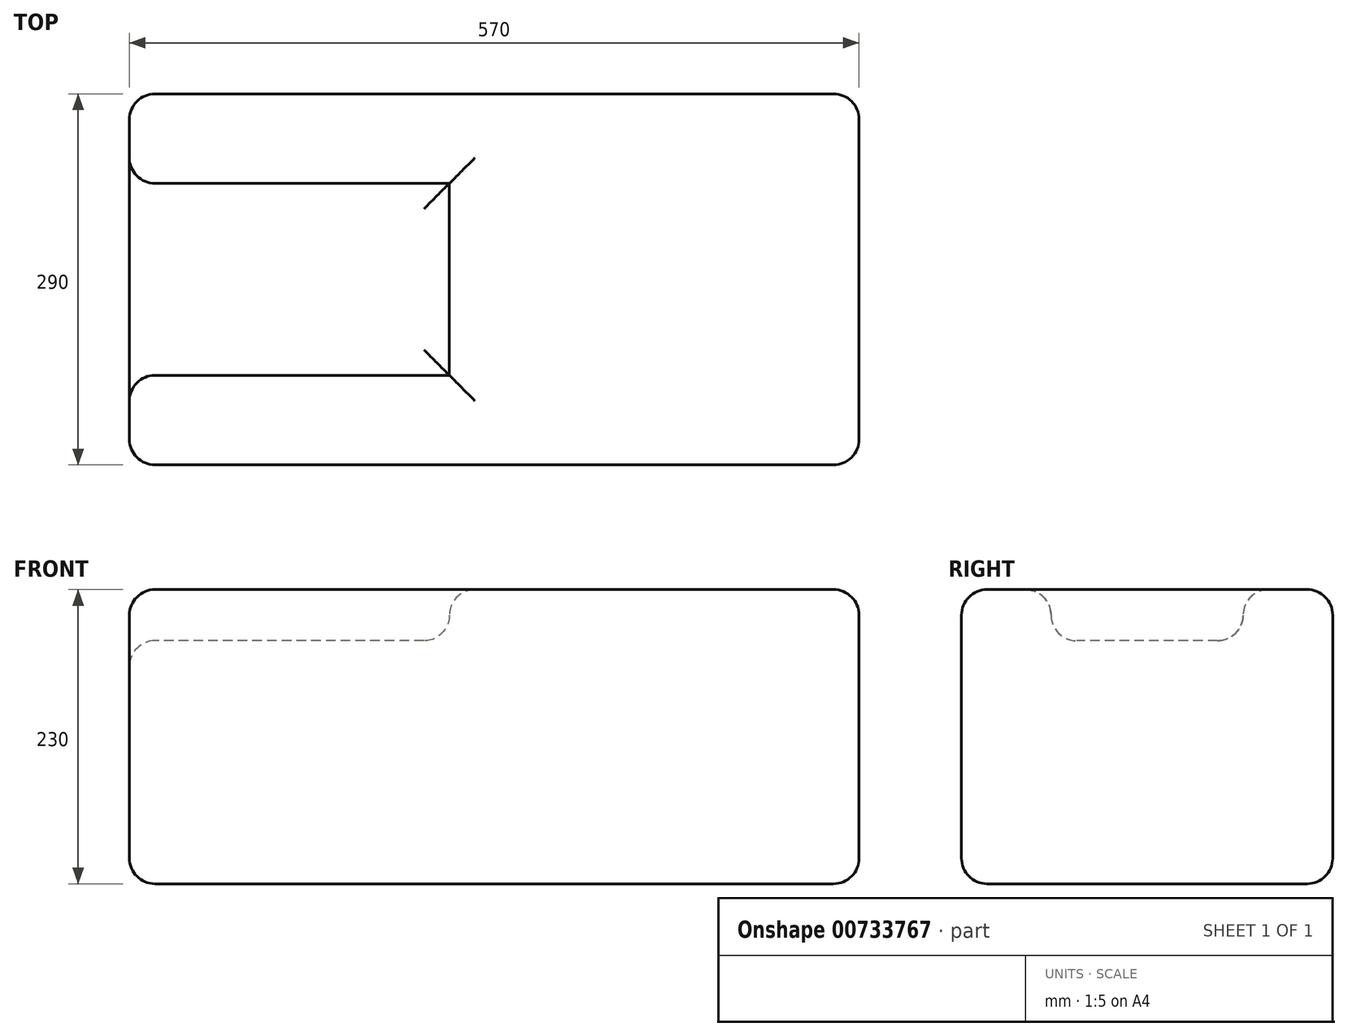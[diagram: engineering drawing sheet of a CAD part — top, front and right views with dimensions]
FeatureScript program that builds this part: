
annotation { "Feature Type Name" : "Feature", "Feature Type Description" : "" }
export const myFeature = defineFeature(function(context is Context, id is Id, definition is map)
    precondition{}
    {
        {
            var Q0;
            Q0=qCreatedBy(makeId("Top.planeOp"),FACE);
            var sketch = newSketch(context, id + "F0", { "sketchPlane" : qUnion([Q0])});
            skLineSegment(sketch, "E0.bottom", {"start": v(0, 0) * mm, "end": v(570, 0) * mm});
            skLineSegment(sketch, "E0.top", {"start": v(0, -290) * mm, "end": v(570, -290) * mm});
            skLineSegment(sketch, "E0.left", {"start": v(0, 0) * mm, "end": v(0, -290) * mm});
            skLineSegment(sketch, "E0.right", {"start": v(570, 0) * mm, "end": v(570, -290) * mm});
            skSolve(sketch);
        }
        {
            var Q0;
            Q0=makeQuery(id+"F0.imprint","IMPRINT",FACE,{"disambiguationData":[TD([[makeQuery(id+"F0.imprint","IMPRINT",EDGE,{"derivedFrom":sQuery(id+"F0.wireOp",EDGE,"E0.bottom")}),-1.0]])]});
            extrude(context, id + "F1", {"entities" : qUnion([Q0]), "depth" : 230 * mm, "offsetDistance" : 25 * mm});
        }
        {
            var Q0;
            Q0=makeQuery(id+"F1.opExtrude","CAP_FACE",FACE,{"disambiguationData":[OSD([sQuery(id+"F0.wireOp",EDGE,"E0.bottom"),sQuery(id+"F0.wireOp",EDGE,"E0.top"),sQuery(id+"F0.wireOp",EDGE,"E0.left"),sQuery(id+"F0.wireOp",EDGE,"E0.right")])],"isStart":false});
            var sketch = newSketch(context, id + "F2", { "sketchPlane" : qUnion([Q0])});
            skLineSegment(sketch, "E1.top", {"start": v(250, -220) * mm, "end": v(0, -220) * mm});
            skLineSegment(sketch, "E1.left", {"start": v(250, -145) * mm, "end": v(250, -220) * mm});
            skLineSegment(sketch, "E1.right", {"start": v(0, -145) * mm, "end": v(0, -220) * mm});
            skLineSegment(sketch, "E2.MirrorCS", {"start": v(250, -70) * mm, "end": v(0, -70) * mm});
            skLineSegment(sketch, "E3", {"start": v(250, -145) * mm, "end": v(250, -70) * mm});
            skSolve(sketch);
        }
        {
            var Q0;
            Q0=makeQuery(id+"F2.imprint","IMPRINT",FACE,{"disambiguationData":[TD([[makeQuery(id+"F2.imprint","IMPRINT",EDGE,{"derivedFrom":sQuery(id+"F2.wireOp",EDGE,"E1.top")}),-1.0]])]});
            extrude(context, id + "F3", {"entities" : qUnion([Q0]), "operationType" : NewBodyOperationType.REMOVE, "oppositeDirection" : true, "depth" : 40 * mm, "offsetDistance" : 25 * mm});
        }
        {
            var Q0;
            Q0=makeQuery(id+"F1.opExtrude","SWEPT_FACE",FACE,{"disambiguationData":[OSD([sQuery(id+"F0.wireOp",EDGE,"E0.left")])]});
            var Q1;
            Q1=makeQuery(id+"F1.opExtrude","SWEPT_FACE",FACE,{"disambiguationData":[OSD([sQuery(id+"F0.wireOp",EDGE,"E0.right")])]});
            var Q2;
            Q2=makeQuery(id+"F1.opExtrude","SWEPT_FACE",FACE,{"disambiguationData":[OSD([sQuery(id+"F0.wireOp",EDGE,"E0.top")])]});
            var Q3;
            Q3=makeQuery(id+"F1.opExtrude","SWEPT_FACE",FACE,{"disambiguationData":[OSD([sQuery(id+"F0.wireOp",EDGE,"E0.bottom")])]});
            var Q4;
            Q4=makeQuery(id+"F3.boolean.opBoolean","COPY",FACE,{"derivedFrom":makeQuery(id+"F3.opExtrude","CAP_FACE",FACE,{"disambiguationData":[OSD([sQuery(id+"F0.wireOp",EDGE,"E0.left"),sQuery(id+"F2.wireOp",EDGE,"E1.top"),sQuery(id+"F2.wireOp",EDGE,"E1.left"),sQuery(id+"F2.wireOp",EDGE,"E1.right"),sQuery(id+"F2.wireOp",EDGE,"E2.MirrorCS"),sQuery(id+"F2.wireOp",EDGE,"E3")])],"isStart":false})});
            var Q5;
            Q5=makeQuery(id+"F3.boolean.opBoolean","COPY",EDGE,{"derivedFrom":makeQuery(id+"F3.opExtrude","CAP_EDGE",EDGE,{"disambiguationData":[OSD([sQuery(id+"F2.wireOp",EDGE,"E1.top")])],"isStart":true})});
            var Q6;
            Q6=makeQuery(id+"F3.boolean.opBoolean","COPY",EDGE,{"derivedFrom":makeQuery(id+"F3.opExtrude","CAP_EDGE",EDGE,{"disambiguationData":[OSD([sQuery(id+"F2.wireOp",EDGE,"E1.left"),sQuery(id+"F2.wireOp",EDGE,"E3")])],"isStart":true})});
            var Q7;
            Q7=makeQuery(id+"F3.boolean.opBoolean","COPY",EDGE,{"derivedFrom":makeQuery(id+"F3.opExtrude","CAP_EDGE",EDGE,{"disambiguationData":[OSD([sQuery(id+"F2.wireOp",EDGE,"E2.MirrorCS")])],"isStart":true})});
            fillet(context, id + "F4", {"entities" : qUnion([Q0, Q1, Q2, Q3, Q4, Q5, Q6, Q7]), "radius" : 20 * mm, "allowEdgeOverflow" : false});
        }
        {
            var Q0;
            Q0=makeQuery(id+"F3.boolean.opBoolean","COPY",EDGE,{"derivedFrom":makeQuery(id+"F3.opExtrude","CAP_EDGE",EDGE,{"disambiguationData":[OSD([sQuery(id+"F2.wireOp",EDGE,"E2.MirrorCS")])],"isStart":true})});
            var Q1;
            Q1=makeQuery(id+"F3.boolean.opBoolean","COPY",EDGE,{"derivedFrom":makeQuery(id+"F3.opExtrude","CAP_EDGE",EDGE,{"disambiguationData":[OSD([sQuery(id+"F2.wireOp",EDGE,"E1.left"),sQuery(id+"F2.wireOp",EDGE,"E3")])],"isStart":true})});
            var Q2;
            Q2=makeQuery(id+"F3.boolean.opBoolean","COPY",EDGE,{"derivedFrom":makeQuery(id+"F3.opExtrude","CAP_EDGE",EDGE,{"disambiguationData":[OSD([sQuery(id+"F2.wireOp",EDGE,"E1.top")])],"isStart":true})});
            var Q3;
            Q3=makeQuery(id+"F3.boolean.opBoolean","COPY",EDGE,{"derivedFrom":makeQuery(id+"F3.opExtrude","CAP_EDGE",EDGE,{"disambiguationData":[OSD([sQuery(id+"F2.wireOp",EDGE,"E1.left"),sQuery(id+"F2.wireOp",EDGE,"E3")])],"isStart":false})});
            var Q4;
            Q4=makeQuery(id+"F3.boolean.opBoolean","COPY",EDGE,{"derivedFrom":makeQuery(id+"F3.opExtrude","CAP_EDGE",EDGE,{"disambiguationData":[OSD([sQuery(id+"F2.wireOp",EDGE,"E1.top")])],"isStart":false})});
            var Q5;
            Q5=makeQuery(id+"F3.boolean.opBoolean","COPY",EDGE,{"derivedFrom":makeQuery(id+"F3.opExtrude","CAP_EDGE",EDGE,{"disambiguationData":[OSD([sQuery(id+"F2.wireOp",EDGE,"E2.MirrorCS")])],"isStart":false})});
            var Q6;
            {var subQ0=sQuery(id+"F0.wireOp",EDGE,"E0.left");var subQ1=sQuery(id+"F0.wireOp",EDGE,"E0.top");Q6=makeQuery(id+"F3.boolean.opBoolean","SPLIT",EDGE,{"disambiguationData":[TD([makeQuery(id+"F1.opExtrude","SWEPT_FACE",FACE,{"disambiguationData":[OSD([subQ1])]})])],"derivedFrom":makeQuery(id+"F1.opExtrude","CAP_EDGE",EDGE,{"disambiguationData":[OSD([subQ0])],"isStart":false})});}
            var Q7;
            {var subQ0=sQuery(id+"F0.wireOp",EDGE,"E0.bottom");var subQ1=sQuery(id+"F0.wireOp",EDGE,"E0.left");Q7=makeQuery(id+"F3.boolean.opBoolean","SPLIT",EDGE,{"disambiguationData":[TD([makeQuery(id+"F1.opExtrude","SWEPT_FACE",FACE,{"disambiguationData":[OSD([subQ0])]})])],"derivedFrom":makeQuery(id+"F1.opExtrude","CAP_EDGE",EDGE,{"disambiguationData":[OSD([subQ1])],"isStart":false})});}
            var Q8;
            Q8=makeQuery(id+"F1.opExtrude","CAP_EDGE",EDGE,{"disambiguationData":[OSD([sQuery(id+"F0.wireOp",EDGE,"E0.top")])],"isStart":false});
            var Q9;
            Q9=makeQuery(id+"F1.opExtrude","CAP_FACE",FACE,{"disambiguationData":[OSD([sQuery(id+"F0.wireOp",EDGE,"E0.bottom"),sQuery(id+"F0.wireOp",EDGE,"E0.top"),sQuery(id+"F0.wireOp",EDGE,"E0.left"),sQuery(id+"F0.wireOp",EDGE,"E0.right")])],"isStart":false});
            var Q10;
            Q10=makeQuery(id+"F1.opExtrude","SWEPT_EDGE",EDGE,{"disambiguationData":[OSD([sQuery(id+"F0.wireOp",EDGE,"E0.top"),sQuery(id+"F0.wireOp",EDGE,"E0.right")])]});
            var Q11;
            Q11=makeQuery(id+"F1.opExtrude","SWEPT_EDGE",EDGE,{"disambiguationData":[OSD([sQuery(id+"F0.wireOp",EDGE,"E0.bottom"),sQuery(id+"F0.wireOp",EDGE,"E0.right")])]});
            var Q12;
            Q12=makeQuery(id+"F1.opExtrude","CAP_EDGE",EDGE,{"disambiguationData":[OSD([sQuery(id+"F0.wireOp",EDGE,"E0.right")])],"isStart":true});
            var Q13;
            Q13=makeQuery(id+"F1.opExtrude","CAP_EDGE",EDGE,{"disambiguationData":[OSD([sQuery(id+"F0.wireOp",EDGE,"E0.bottom")])],"isStart":true});
            var Q14;
            Q14=makeQuery(id+"F1.opExtrude","SWEPT_EDGE",EDGE,{"disambiguationData":[OSD([sQuery(id+"F0.wireOp",EDGE,"E0.bottom"),sQuery(id+"F0.wireOp",EDGE,"E0.left")])]});
            var Q15;
            Q15=makeQuery(id+"F1.opExtrude","CAP_EDGE",EDGE,{"disambiguationData":[OSD([sQuery(id+"F0.wireOp",EDGE,"E0.left")])],"isStart":true});
            var Q16;
            Q16=makeQuery(id+"F1.opExtrude","CAP_EDGE",EDGE,{"disambiguationData":[OSD([sQuery(id+"F0.wireOp",EDGE,"E0.top")])],"isStart":true});
            var Q17;
            Q17=makeQuery(id+"F1.opExtrude","SWEPT_EDGE",EDGE,{"disambiguationData":[OSD([sQuery(id+"F0.wireOp",EDGE,"E0.top"),sQuery(id+"F0.wireOp",EDGE,"E0.left")])]});
            var Q18;
            Q18=makeQuery(id+"F3.boolean.opBoolean","COPY",EDGE,{"derivedFrom":makeQuery(id+"F3.opExtrude","CAP_EDGE",EDGE,{"disambiguationData":[OSD([sQuery(id+"F0.wireOp",EDGE,"E0.left"),sQuery(id+"F2.wireOp",EDGE,"E1.right")])],"isStart":false})});
            fillet(context, id + "F5", {"entities" : qUnion([Q0, Q1, Q2, Q3, Q4, Q5, Q6, Q7, Q8, Q9, Q10, Q11, Q12, Q13, Q14, Q15, Q16, Q17, Q18]), "radius" : 20 * mm, "tangentPropagation" : true, "allowEdgeOverflow" : false});
        }
    });
